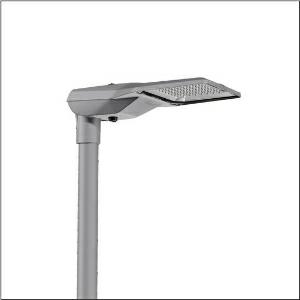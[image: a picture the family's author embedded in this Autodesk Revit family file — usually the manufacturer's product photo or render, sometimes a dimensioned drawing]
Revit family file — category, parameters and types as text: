
# Revit family: streetlight_sl_21_iq_midi___p0_5a_5xe3v31y08nb_ca8d
name_source: partatom
category: Lighting Fixtures
units: mm (PartAtom-declared; Revit-internal decimal feet)

## family parameters
Cut with Voids When Loaded = No
Host = Face
Light Source = No
Part Type = Normal
Room Calculation Point = No
Round Connector Dimension = Use Diameter
Shared = No

## types (1)
- --- (1 x LED, 21180 lm, 136.6 W, 3000K)
    Apparent Load = 137 VA
    CIE Flux Codes = 37 73 96 100 100
    Color Rendering = 70
    Color Temperature = 3000K
    Default Elevation = 1800 mm
    Description = Streetlight SL 21 iQ midi, mast luminaire, primary light control with lens, of PMMA, primary optical cover: cover, of toughened safety glass, transparent, light distribution: P0.5a, light emission: direct distribution, primary light characteristic: asymmetric, installation type: post-top, side-entry, LED, High Power LED, rated luminous flux: 21.180lm, luminous efficacy: 155lm/W, light colour: 730, colour temperature: 3000K, control gear: iQ-Street Remote, D4i with power reduction, control: pre-setting: logarithmic dimming characteristic, Street-Remote, Auto-Match, Temp-Guard, Lumen-Switch, Night-Set, Smart-Wire, Light-Fading, Desk-Remote (wireless, voltage-free reading and setting of iQ features in the workshop via application-optimized NFC function/RFID function), optimised constant luminous flux control (CLO 2.0), mains connection: 230..240V, AC, 50/60Hz, start of lifetime: 137W, end of service life: 144W, reduction: 61W, luminaire housing, of diecast aluminium, powder-coated, SITECO metallic grey (DB 702S), corrosivity category C5 high according to DIN EN ISO 12944, please order mast flange separately, inclination adjustable: 0°, 5°, 10°, 15°, sealing non-destructively replaceable, multi-level sealing system, length: 644mm, width: 335mm, height: 110mm, mast flange for spigot size: 42mm (side-entry): 5XC10008XM4, 60/48mm (side-entry/post-top): 5XC10108XM2, 76/60mm (side-entry/post-top): 5XC10108XM1, mounting height: 4..8m, Smart Interface below and above, protection rating (complete): IP66, insulation class (complete): insulation class II (safety insulation), certification: CE, ENEC, ENEC+, VDE, impact resistance: IK10, permissible operating ambient temperature for outdoor applications: -40..+50°C, standard-compliant lighting for roads and squares, packaging unit: 1 piece

Light Distribution: P0.5a
    Height = 111 mm
    Lamp = 1 x LED
    Lamp Light Flux = 21180 lm
    Lamp Power = 136.6 W
    Lamp count = 1
    Length = 644 mm
    Luminous efficacy = 155 lm/W
    Manufacturer = Siteco
    ModVariant = No
    Model = 5XE3V31Y08NB
    Number of Poles = 1
    OnlyDefault = Yes
    Power Factor = 1
    Product Name = Streetlight SL 21 iQ midi | P0.5a
    Product group = mast luminaire | pylon top
    ProductGroupID = 6100
    Protection Class = Protection class II
    Protection Degree = IP 66
    RLX_Detail_Level = 1
    RLX_Emergency_Light_Flux = 0 lm
    RLX_Emergency_Type = 0
    RLX_Emergency_Type_DB = No
    RlxData = <blob elided: 90949 chars, md5=8c09ad00>
    Socket = socket
    Standby Power = 0 W
    System Light Flux = 21180 lm
    System Power = 137 W
    Type Comments = factory setting: luminous flux: 100 % | dim-lin: 254 | 733 mA
    Type Image = l_1004304.jpg
    URL = http://relux.com
    VarID = @adj_077015
    Voltage = 0 V
    Weight = 0.00 kg
    Width = 336 mm

## geometry (parser evidence)
native form markers: Blend x4, Sweep x12
no freeform markers — native parametric forms only
